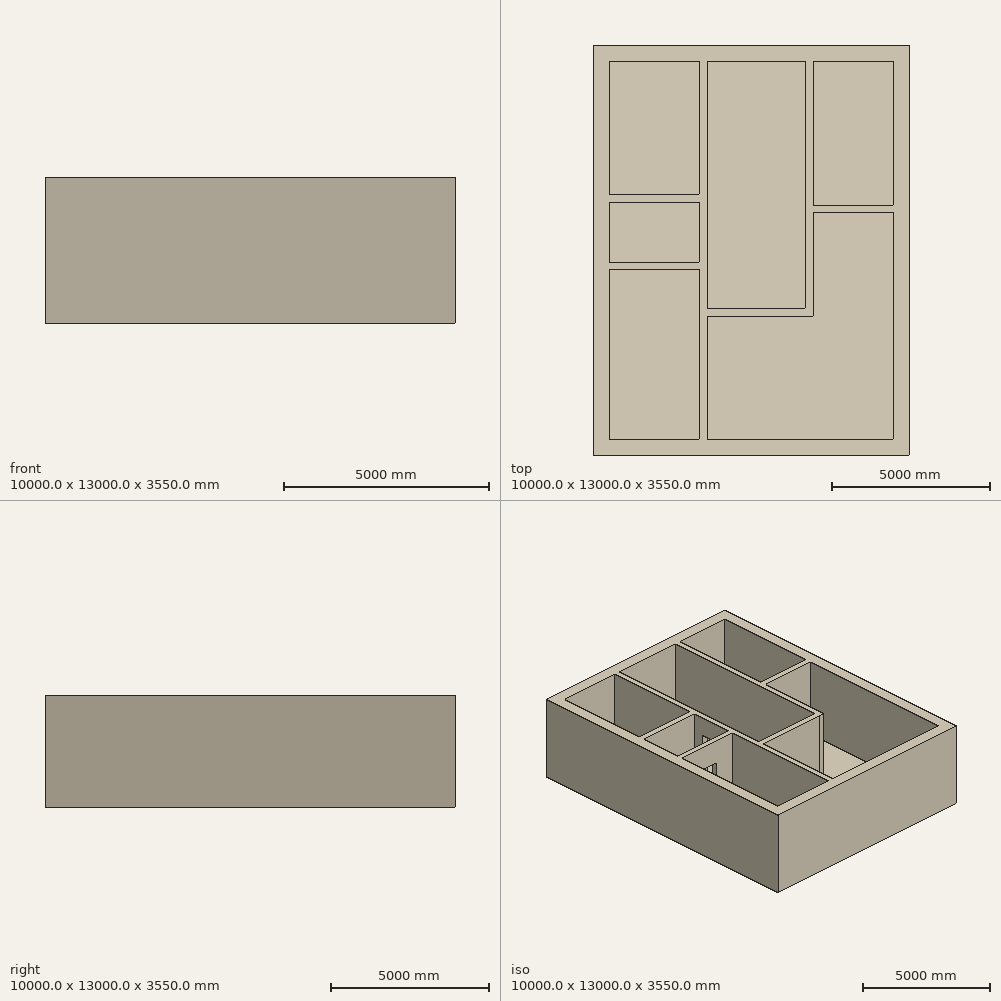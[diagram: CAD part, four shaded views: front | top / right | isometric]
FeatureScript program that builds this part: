
annotation { "Feature Type Name" : "Feature", "Feature Type Description" : "" }
export const myFeature = defineFeature(function(context is Context, id is Id, definition is map)
    precondition{}
    {
        {
            var Q0;
            Q0=qCreatedBy(makeId("Top.planeOp"),FACE);
            var sketch = newSketch(context, id + "F0", { "sketchPlane" : qUnion([Q0])});
            skLineSegment(sketch, "E0.bottom", {"start": v(5000, 6500) * mm, "end": v(-5000, 6500) * mm});
            skLineSegment(sketch, "E0.top", {"start": v(5000, -6500) * mm, "end": v(-5000, -6500) * mm});
            skLineSegment(sketch, "E0.left", {"start": v(5000, 6500) * mm, "end": v(5000, -6500) * mm});
            skLineSegment(sketch, "E0.right", {"start": v(-5000, 6500) * mm, "end": v(-5000, -6500) * mm});
            skPoint(sketch, "E0.middle", {"position": v(0, 0) * mm});
            skSolve(sketch);
        }
        {
            var Q0;
            Q0=qSketchRegion(id+"F0",true);
            extrude(context, id + "F1", {"entities" : qUnion([Q0]), "depth" : 3550 * mm, "offsetDistance" : 25 * mm});
        }
        {
            var Q0;
            Q0=makeQuery(id+"F1.opExtrude","CAP_FACE",FACE,{"disambiguationData":[OSD([sQuery(id+"F0.wireOp",EDGE,"E0.bottom"),sQuery(id+"F0.wireOp",EDGE,"E0.top"),sQuery(id+"F0.wireOp",EDGE,"E0.left"),sQuery(id+"F0.wireOp",EDGE,"E0.right")])],"isStart":false});
            var sketch = newSketch(context, id + "F2", { "sketchPlane" : qUnion([Q0])});
            skLineSegment(sketch, "E1.0", {"start": v(-4500, 6000) * mm, "end": v(-4500, -6000) * mm});
            skLineSegment(sketch, "E1.1", {"start": v(4500, 6000) * mm, "end": v(-4500, 6000) * mm});
            skLineSegment(sketch, "E1.2", {"start": v(4500, 6000) * mm, "end": v(4500, -6000) * mm});
            skLineSegment(sketch, "E1.3", {"start": v(4500, -6000) * mm, "end": v(-4500, -6000) * mm});
            skSolve(sketch);
        }
        {
            var Q0;
            Q0=qSketchRegion(id+"F2",true);
            var Q1;
            Q1=makeQuery(id+"F2.imprint","IMPRINT",FACE,{"disambiguationData":[TD([[makeQuery(id+"F2.imprint","IMPRINT",EDGE,{"derivedFrom":sQuery(id+"F2.wireOp",EDGE,"6241154e-0bf6-49ba-bd71-02362f76f25d.0")}),1.0]])]});
            extrude(context, id + "F3", {"entities" : qUnion([Q0, Q1]), "operationType" : NewBodyOperationType.REMOVE, "oppositeDirection" : true, "depth" : 3300 * mm, "offsetDistance" : 25 * mm});
        }
        {
            var Q0;
            Q0=makeQuery(id+"F3.boolean.opBoolean","COPY",FACE,{"derivedFrom":makeQuery(id+"F3.opExtrude","CAP_FACE",FACE,{"disambiguationData":[OSD([sQuery(id+"F2.wireOp",EDGE,"E1.0"),sQuery(id+"F2.wireOp",EDGE,"E1.1"),sQuery(id+"F2.wireOp",EDGE,"E1.2"),sQuery(id+"F2.wireOp",EDGE,"E1.3")])],"isStart":false})});
            var sketch = newSketch(context, id + "F4", { "sketchPlane" : qUnion([Q0])});
            skLineSegment(sketch, "E2", {"start": v(-4500, -366.62) * mm, "end": v(-1660.5, -366.62) * mm});
            skLineSegment(sketch, "E3", {"start": v(-1660.5, -616.62) * mm, "end": v(-1660.5, -6000) * mm});
            skLineSegment(sketch, "E4", {"start": v(-1660.5, -366.62) * mm, "end": v(-1660.5, 1531.45) * mm});
            skLineSegment(sketch, "E5", {"start": v(-1660.5, 1531.45) * mm, "end": v(-4500, 1531.45) * mm});
            skLineSegment(sketch, "E6", {"start": v(-4500, 1531.45) * mm, "end": v(-1660.5, 1531.45) * mm});
            skLineSegment(sketch, "E7", {"start": v(-1660.5, 1781.45) * mm, "end": v(-1660.5, 6000) * mm});
            skLineSegment(sketch, "E8", {"start": v(1725.2, 1441.9) * mm, "end": v(1725.2, 6000) * mm});
            skLineSegment(sketch, "E9", {"start": v(1975.2, 1441.9) * mm, "end": v(4500, 1441.9) * mm});
            skLineSegment(sketch, "E10", {"start": v(1725.2, 1441.9) * mm, "end": v(1725.2, -1827.54) * mm});
            skLineSegment(sketch, "E11", {"start": v(-1410.5, -2077.54) * mm, "end": v(1725.2, -2077.54) * mm});
            skLineSegment(sketch, "E12.0", {"start": v(-4500, -616.62) * mm, "end": v(-1660.5, -616.62) * mm});
            skLineSegment(sketch, "E13.0", {"start": v(-1410.5, 6000) * mm, "end": v(-1410.5, -1827.54) * mm});
            skLineSegment(sketch, "E14.0", {"start": v(-4500, 1781.45) * mm, "end": v(-1660.5, 1781.45) * mm});
            skLineSegment(sketch, "E15.0", {"start": v(-1410.5, -1827.54) * mm, "end": v(1725.2, -1827.54) * mm});
            skLineSegment(sketch, "E16.trimOffspring", {"start": v(-1410.5, -2077.54) * mm, "end": v(-1410.5, -6000) * mm});
            skLineSegment(sketch, "E17.0", {"start": v(1975.2, 1441.9) * mm, "end": v(1975.2, 6000) * mm});
            skLineSegment(sketch, "E18.0", {"start": v(1975.19, 1191.9) * mm, "end": v(4500, 1191.9) * mm});
            skLineSegment(sketch, "E19.0", {"start": v(1975.19, 1191.9) * mm, "end": v(1975.13, -2083.27) * mm});
            skLineSegment(sketch, "E20", {"start": v(1975.13, -2083.27) * mm, "end": v(1725.2, -2077.54) * mm});
            skLineSegment(sketch, "E21", {"start": v(4500, 1191.9) * mm, "end": v(4500, 1441.9) * mm});
            skLineSegment(sketch, "E22", {"start": v(1975.2, 6000) * mm, "end": v(1725.2, 6000) * mm});
            skLineSegment(sketch, "E23", {"start": v(-1410.5, 6000) * mm, "end": v(-1660.5, 6000) * mm});
            skLineSegment(sketch, "E24", {"start": v(-4500, 1781.45) * mm, "end": v(-4500, 1531.45) * mm});
            skLineSegment(sketch, "E25", {"start": v(-4500, -366.62) * mm, "end": v(-4500, -616.62) * mm});
            skLineSegment(sketch, "E26", {"start": v(-1660.5, -6000) * mm, "end": v(-1410.5, -6000) * mm});
            skSolve(sketch);
        }
        {
            var Q0;
            Q0=makeQuery(id+"F4.imprint","IMPRINT",FACE,{"disambiguationData":[TD([[makeQuery(id+"F4.imprint","IMPRINT",EDGE,{"derivedFrom":sQuery(id+"F4.wireOp",EDGE,"E2")}),-1.0]])]});
            extrude(context, id + "F5", {"entities" : qUnion([Q0]), "operationType" : NewBodyOperationType.ADD, "depth" : 3300 * mm, "offsetDistance" : 25 * mm});
        }
        {
            var Q0;
            Q0=makeQuery(id+"F5.opExtrude","SWEPT_FACE",FACE,{"disambiguationData":[OSD([sQuery(id+"F4.wireOp",EDGE,"E12.0")])]});
            var sketch = newSketch(context, id + "F6", { "sketchPlane" : qUnion([Q0])});
            skLineSegment(sketch, "E27.bottom", {"start": v(-3580.25, 250) * mm, "end": v(-2580.25, 250) * mm});
            skLineSegment(sketch, "E27.top", {"start": v(-3580.25, 2550) * mm, "end": v(-2580.25, 2550) * mm});
            skLineSegment(sketch, "E27.left", {"start": v(-3580.25, 250) * mm, "end": v(-3580.25, 2550) * mm});
            skLineSegment(sketch, "E27.right", {"start": v(-2580.25, 250) * mm, "end": v(-2580.25, 2550) * mm});
            skLineSegment(sketch, "E28", {"start": v(-3580.25, 2550) * mm, "end": v(-4500, 2550) * mm, "construction": true});
            skLineSegment(sketch, "E29", {"start": v(-2580.25, 2550) * mm, "end": v(-1660.5, 2550) * mm, "construction": true});
            skSolve(sketch);
        }
        {
            var Q0;
            Q0=makeQuery(id+"F6.imprint","IMPRINT",FACE,{"disambiguationData":[TD([[makeQuery(id+"F6.imprint","IMPRINT",EDGE,{"derivedFrom":sQuery(id+"F6.wireOp",EDGE,"E27.bottom")}),1.0]])]});
            extrude(context, id + "F7", {"entities" : qUnion([Q0]), "operationType" : NewBodyOperationType.REMOVE, "oppositeDirection" : true, "depth" : 250 * mm, "offsetDistance" : 25 * mm});
        }
        {
            var Q0;
            Q0=makeQuery(id+"F5.opExtrude","SWEPT_FACE",FACE,{"disambiguationData":[OSD([sQuery(id+"F4.wireOp",EDGE,"E4")])]});
            var sketch = newSketch(context, id + "F8", { "sketchPlane" : qUnion([Q0])});
            skLineSegment(sketch, "E30.bottom", {"start": v(-82.41, 250) * mm, "end": v(-1082.41, 250) * mm});
            skLineSegment(sketch, "E30.top", {"start": v(-82.41, 2750) * mm, "end": v(-1082.41, 2750) * mm});
            skLineSegment(sketch, "E30.left", {"start": v(-82.41, 250) * mm, "end": v(-82.41, 2750) * mm});
            skLineSegment(sketch, "E30.right", {"start": v(-1082.41, 250) * mm, "end": v(-1082.41, 2750) * mm});
            skLineSegment(sketch, "E31", {"start": v(-1082.41, 2750) * mm, "end": v(-1531.45, 2750) * mm, "construction": true});
            skLineSegment(sketch, "E32", {"start": v(-82.41, 2750) * mm, "end": v(366.62, 2750) * mm, "construction": true});
            skSolve(sketch);
        }
        {
            var Q0;
            Q0=qSketchRegion(id+"F8",true);
            var Q1;
            Q1=makeQuery(id+"F5.opExtrude","SWEPT_FACE",FACE,{"disambiguationData":[OSD([sQuery(id+"F4.wireOp",EDGE,"E13.0")])]});
            extrude(context, id + "F9", {"entities" : qUnion([Q0]), "operationType" : NewBodyOperationType.REMOVE, "endBound" : BoundingType.UP_TO_SURFACE, "oppositeDirection" : true, "depth" : 25 * mm, "endBoundEntityFace" : qUnion([Q1]), "offsetDistance" : 25 * mm});
        }
    });
